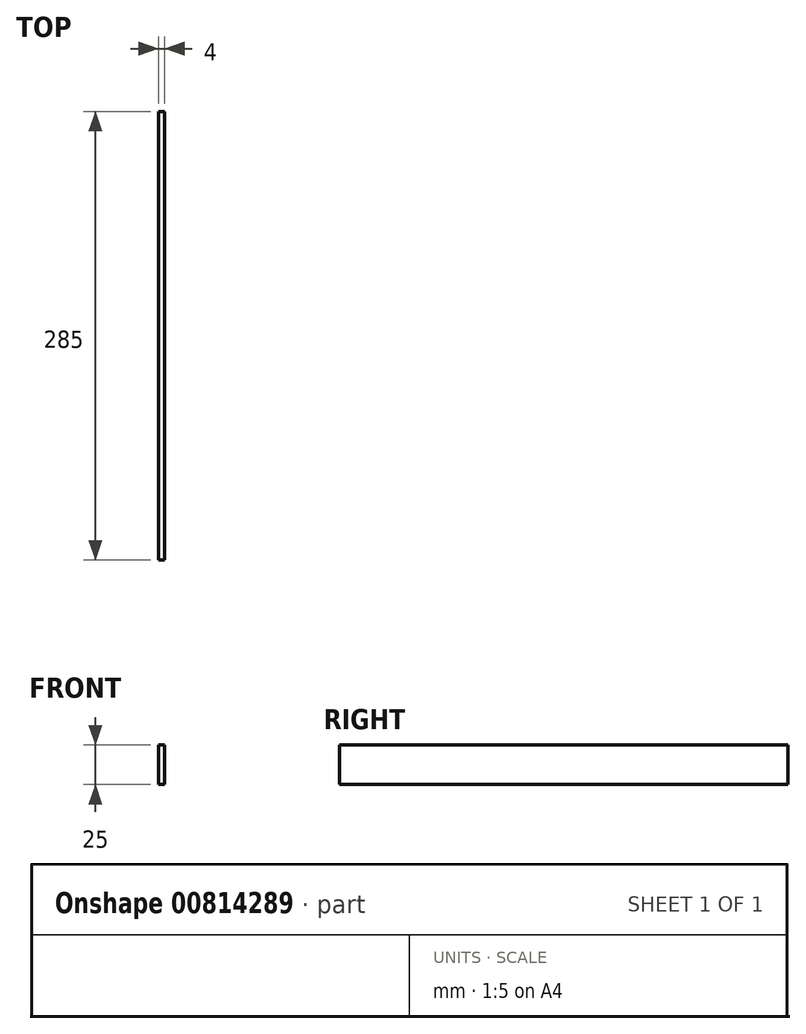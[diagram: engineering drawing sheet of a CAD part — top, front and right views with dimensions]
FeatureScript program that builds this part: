
annotation { "Feature Type Name" : "Feature", "Feature Type Description" : "" }
export const myFeature = defineFeature(function(context is Context, id is Id, definition is map)
    precondition{}
    {
        {
            var Q0;
            Q0=qCreatedBy(makeId("Front.planeOp"),FACE);
            var sketch = newSketch(context, id + "F0", { "sketchPlane" : qUnion([Q0])});
            skLineSegment(sketch, "E0.bottom", {"start": v(2, 12.5) * mm, "end": v(-2, 12.5) * mm});
            skLineSegment(sketch, "E0.top", {"start": v(2, -12.5) * mm, "end": v(-2, -12.5) * mm});
            skLineSegment(sketch, "E0.left", {"start": v(2, 12.5) * mm, "end": v(2, -12.5) * mm});
            skLineSegment(sketch, "E0.right", {"start": v(-2, 12.5) * mm, "end": v(-2, -12.5) * mm});
            skPoint(sketch, "E0.middle", {"position": v(0, 0) * mm});
            skLineSegment(sketch, "E1.bottom", {"start": v(2, 12.5) * mm, "end": v(2, 12.5) * mm});
            skLineSegment(sketch, "E1.top", {"start": v(2, 9.5) * mm, "end": v(2, 9.5) * mm});
            skLineSegment(sketch, "E1.left", {"start": v(2, 12.5) * mm, "end": v(2, 9.5) * mm});
            skLineSegment(sketch, "E1.right", {"start": v(2, 12.5) * mm, "end": v(2, 9.5) * mm});
            skSolve(sketch);
        }
        {
            var Q0;
            Q0=makeQuery(id+"F0.imprint","IMPRINT",FACE,{"disambiguationData":[TD([[makeQuery(id+"F0.imprint","IMPRINT",EDGE,{"derivedFrom":sQuery(id+"F0.wireOp",EDGE,"E1.bottom")}),-1.0]])]});
            var Q1;
            Q1=makeQuery(id+"F0.imprint","IMPRINT",FACE,{"disambiguationData":[TD([[makeQuery(id+"F0.imprint","IMPRINT",EDGE,{"derivedFrom":sQuery(id+"F0.wireOp",EDGE,"E0.bottom")}),1.0]])]});
            extrude(context, id + "F1", {"entities" : qUnion([Q0, Q1]), "depth" : 285 * mm, "offsetDistance" : 25 * mm, "symmetric" : true});
        }
    });
